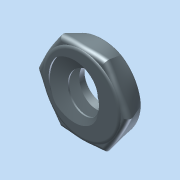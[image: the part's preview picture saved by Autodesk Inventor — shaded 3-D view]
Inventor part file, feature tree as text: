
AUTODESK INVENTOR PART (.ipt)
format: ipt  version: 2015 (Build 190159000, 159)  size: 637,440 bytes
history: native  units: in
note: dims shown in document units (in); Inventor stores cm internally (conversion verified against a paired STEP export)
features: other x2, plane x2, sketch x2, imported_body x1
ambient origin geometry x8: Origin, YZ Plane, XZ Plane, XY Plane, X Axis, Y Axis, Z Axis, Center Point
bodies: Body1 (feature_tree)
feature tree (7):
  other  "Nut"
  other  "Nut.ipt1"
  plane  "Work Plane1"
  plane  "Work Plane2"
  sketch  "3D Sketch1"
  sketch  "3D Sketch2"
  imported_body  "Base1"
